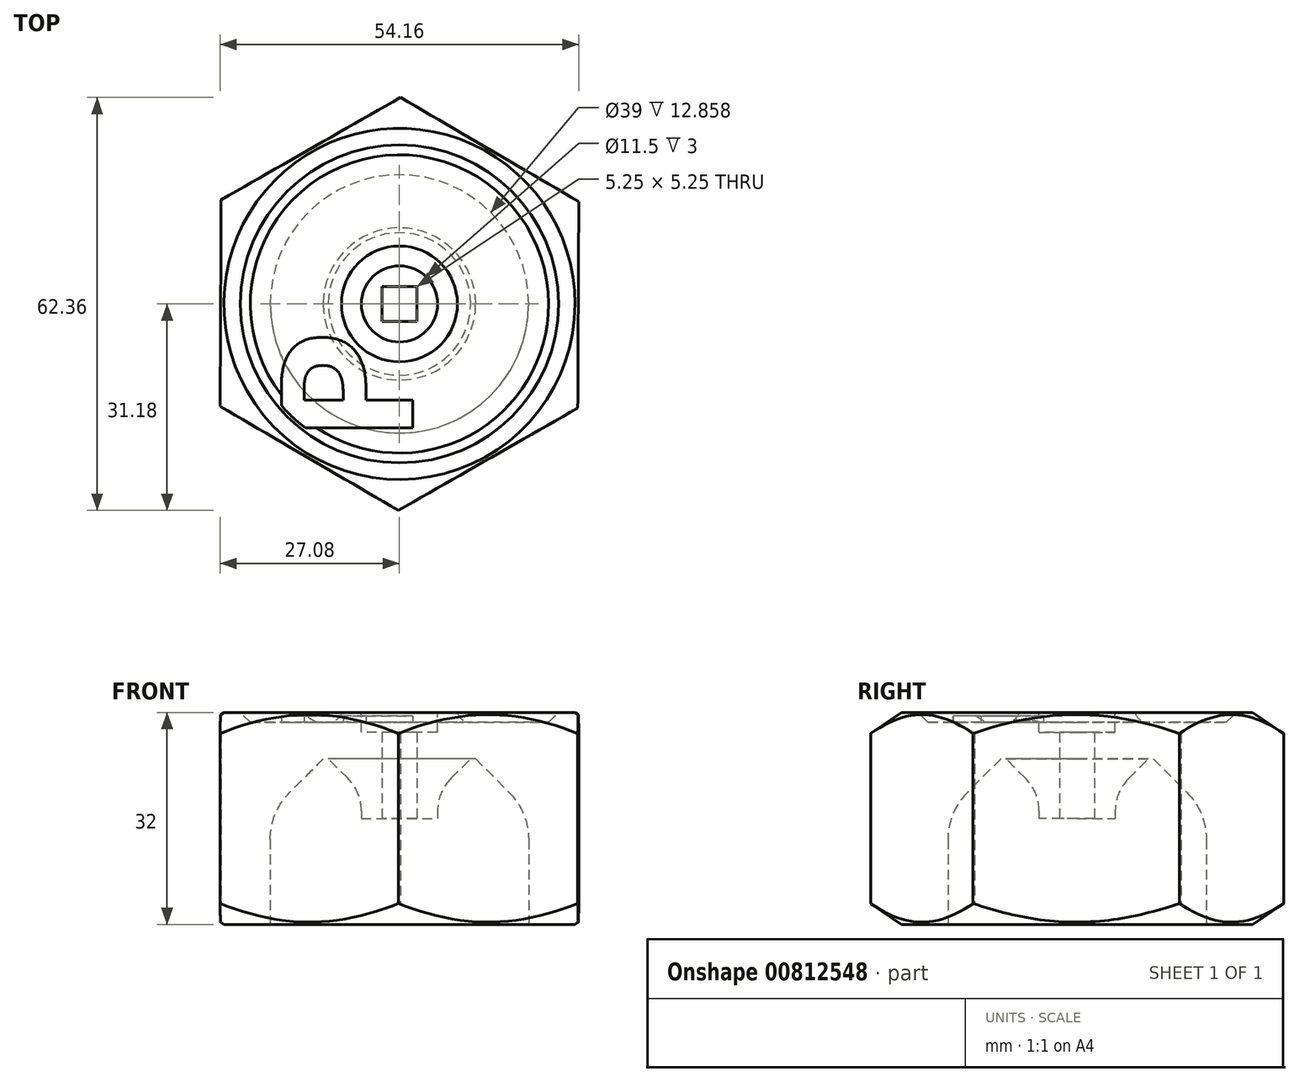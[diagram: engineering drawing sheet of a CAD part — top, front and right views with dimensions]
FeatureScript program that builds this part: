
annotation { "Feature Type Name" : "Feature", "Feature Type Description" : "" }
export const myFeature = defineFeature(function(context is Context, id is Id, definition is map)
    precondition{}
    {
        {
            var Q0;
            Q0=qCreatedBy(makeId("Top.planeOp"),FACE);
            var sketch = newSketch(context, id + "F0", { "sketchPlane" : qUnion([Q0])});
            skCircle(sketch, "E0.cCircle", {"center": v(0, 0) * mm, "radius": 27 * mm, "construction": true});
            skLineSegment(sketch, "E0.0", {"start": v(0.16, 31.18) * mm, "end": v(27.08, 15.45) * mm});
            skLineSegment(sketch, "E0.1", {"start": v(27.08, 15.45) * mm, "end": v(26.92, -15.72) * mm});
            skLineSegment(sketch, "E0.2", {"start": v(26.92, -15.72) * mm, "end": v(-0.16, -31.18) * mm});
            skLineSegment(sketch, "E0.3", {"start": v(-0.16, -31.18) * mm, "end": v(-27.08, -15.45) * mm});
            skLineSegment(sketch, "E0.4", {"start": v(-27.08, -15.45) * mm, "end": v(-26.92, 15.72) * mm});
            skLineSegment(sketch, "E0.5", {"start": v(-26.92, 15.72) * mm, "end": v(0.16, 31.18) * mm});
            skPoint(sketch, "E0.0.midPoint", {"position": v(13.62, 23.31) * mm});
            skLineSegment(sketch, "E1.bottom", {"start": v(2.63, 2.63) * mm, "end": v(-2.62, 2.63) * mm});
            skLineSegment(sketch, "E1.top", {"start": v(2.62, -2.63) * mm, "end": v(-2.62, -2.63) * mm});
            skLineSegment(sketch, "E1.left", {"start": v(2.62, 2.63) * mm, "end": v(2.62, -2.63) * mm});
            skLineSegment(sketch, "E1.right", {"start": v(-2.62, 2.62) * mm, "end": v(-2.62, -2.63) * mm});
            skCircle(sketch, "E2", {"center": v(0, 0) * mm, "radius": 5.75 * mm});
            skSolve(sketch);
        }
        {
            var Q0;
            Q0=makeQuery(id+"F0.imprint","IMPRINT",FACE,{"disambiguationData":[TD([[makeQuery(id+"F0.imprint","IMPRINT",EDGE,{"derivedFrom":sQuery(id+"F0.wireOp",EDGE,"E0.0")}),-1.0]])]});
            var Q1;
            Q1=makeQuery(id+"F0.imprint","IMPRINT",FACE,{"disambiguationData":[TD([[makeQuery(id+"F0.imprint","IMPRINT",EDGE,{"derivedFrom":sQuery(id+"F0.wireOp",EDGE,"E1.bottom")}),-1.0]])]});
            extrude(context, id + "F1", {"entities" : qUnion([Q0, Q1]), "endBound" : BoundingType.SYMMETRIC, "depth" : 32 * mm, "offsetDistance" : 25 * mm});
        }
        {
            var Q0;
            Q0=qCreatedBy(makeId("Front.planeOp"),FACE);
            var sketch = newSketch(context, id + "F2", { "sketchPlane" : qUnion([Q0])});
            skLineSegment(sketch, "E3", {"start": v(0, -34) * mm, "end": v(0, 34) * mm, "construction": true});
            skLineSegment(sketch, "E4", {"start": v(0, 34) * mm, "end": v(50.08, 0) * mm});
            skLineSegment(sketch, "E5", {"start": v(50.08, 0) * mm, "end": v(0, -34) * mm});
            skLineSegment(sketch, "E6", {"start": v(68.47, 39) * mm, "end": v(68.47, -39) * mm});
            skLineSegment(sketch, "E7", {"start": v(0, 34) * mm, "end": v(0, 39) * mm});
            skLineSegment(sketch, "E8", {"start": v(0, 39) * mm, "end": v(68.47, 39) * mm});
            skLineSegment(sketch, "E9", {"start": v(0, -34) * mm, "end": v(0, -40) * mm});
            skLineSegment(sketch, "E10", {"start": v(0, -34) * mm, "end": v(0, -39) * mm});
            skLineSegment(sketch, "E11", {"start": v(0, -39) * mm, "end": v(68.47, -39) * mm});
            skSolve(sketch);
        }
        {
            var Q0;
            Q0=qCreatedBy(makeId("Front.planeOp"),FACE);
            var sketch = newSketch(context, id + "F3", { "sketchPlane" : qUnion([Q0])});
            skLineSegment(sketch, "E12", {"start": v(0, 59.86) * mm, "end": v(0, -69.92) * mm, "construction": true});
            skSolve(sketch);
        }
        {
            var Q0;
            Q0 = qSketchRegion(id + "F2", true);
            var Q1;
            Q1=sQuery(id+"F3.wireOp",EDGE,"E12");
            revolve(context, id + "F4", {"operationType" : NewBodyOperationType.REMOVE, "surfaceOperationType" : NewSurfaceOperationType.NEW, "entities" : qUnion([Q0]), "axis" : qUnion([Q1]), "revolveType" : RevolveType.ONE_DIRECTION, "oppositeDirection" : true, "angle" : 360 * degree});
        }
        {
            var Q0;
            Q0=makeQuery(id+"F1.opExtrude","CAP_FACE",FACE,{"disambiguationData":[OSD([sQuery(id+"F0.wireOp",EDGE,"E0.0"),sQuery(id+"F0.wireOp",EDGE,"E0.1"),sQuery(id+"F0.wireOp",EDGE,"E0.2"),sQuery(id+"F0.wireOp",EDGE,"E0.3"),sQuery(id+"F0.wireOp",EDGE,"E0.4"),sQuery(id+"F0.wireOp",EDGE,"E0.5"),sQuery(id+"F0.wireOp",EDGE,"E1.bottom"),sQuery(id+"F0.wireOp",EDGE,"E1.top"),sQuery(id+"F0.wireOp",EDGE,"E1.left"),sQuery(id+"F0.wireOp",EDGE,"E1.right")])],"isStart":true});
            var sketch = newSketch(context, id + "F5", { "sketchPlane" : qUnion([Q0])});
            skCircle(sketch, "E13", {"center": v(0, 0) * mm, "radius": 19.5 * mm});
            skSolve(sketch);
        }
        {
            var Q0;
            Q0=makeQuery(id+"F5.imprint","IMPRINT",FACE,{"disambiguationData":[TD([[makeQuery(id+"F5.imprint","IMPRINT",EDGE,{"derivedFrom":sQuery(id+"F5.wireOp",EDGE,"E13")}),1.0]])]});
            var Q1;
            Q1=makeQuery(id+"F1.opExtrude","CAP_FACE",FACE,{"disambiguationData":[OSD([sQuery(id+"F0.wireOp",EDGE,"E0.0"),sQuery(id+"F0.wireOp",EDGE,"E0.1"),sQuery(id+"F0.wireOp",EDGE,"E0.2"),sQuery(id+"F0.wireOp",EDGE,"E0.3"),sQuery(id+"F0.wireOp",EDGE,"E0.4"),sQuery(id+"F0.wireOp",EDGE,"E0.5"),sQuery(id+"F0.wireOp",EDGE,"E1.bottom"),sQuery(id+"F0.wireOp",EDGE,"E1.top"),sQuery(id+"F0.wireOp",EDGE,"E1.left"),sQuery(id+"F0.wireOp",EDGE,"E1.right")])],"isStart":false});
            extrude(context, id + "F6", {"entities" : qUnion([Q0]), "operationType" : NewBodyOperationType.REMOVE, "endBound" : BoundingType.UP_TO_SURFACE, "oppositeDirection" : true, "depth" : 25 * mm, "endBoundEntityFace" : qUnion([Q1]), "hasOffset" : true, "offsetDistance" : 7 * mm});
        }
        {
            var Q0;
            Q0=makeQuery(id+"F6.boolean.opBoolean","COPY",EDGE,{"derivedFrom":makeQuery(id+"F6.opExtrude","CAP_EDGE",EDGE,{"disambiguationData":[OSD([sQuery(id+"F5.wireOp",EDGE,"E13")])],"isStart":false})});
            chamfer(context, id + "F7", {"entities" : qUnion([Q0]), "width" : 8 * mm, "tangentPropagation" : true});
        }
        {
            var Q0;
            {var subQ0=sQuery(id+"F5.wireOp",EDGE,"E13");Q0=makeQuery(id+"F7.opChamfer","BLEND_EDGE",EDGE,{"blendedFrom":[makeQuery(id+"F6.boolean.opBoolean","COPY",EDGE,{"derivedFrom":makeQuery(id+"F6.opExtrude","CAP_EDGE",EDGE,{"disambiguationData":[OSD([subQ0])],"isStart":false})}),makeQuery(id+"F6.boolean.opBoolean","COPY",FACE,{"derivedFrom":makeQuery(id+"F6.opExtrude","SWEPT_FACE",FACE,{"disambiguationData":[OSD([subQ0])]})})],"blendedInto":[makeQuery(id+"F6.boolean.opBoolean","COPY",FACE,{"derivedFrom":makeQuery(id+"F6.opExtrude","SWEPT_FACE",FACE,{"disambiguationData":[OSD([subQ0])]})})]});}
            fillet(context, id + "F8", {"entities" : qUnion([Q0]), "radius" : 10 * mm, "tangentPropagation" : true, "allowEdgeOverflow" : false});
        }
        {
            var Q0;
            Q0=makeQuery(id+"F1.opExtrude","CAP_FACE",FACE,{"disambiguationData":[OSD([sQuery(id+"F0.wireOp",EDGE,"E0.0"),sQuery(id+"F0.wireOp",EDGE,"E0.1"),sQuery(id+"F0.wireOp",EDGE,"E0.2"),sQuery(id+"F0.wireOp",EDGE,"E0.3"),sQuery(id+"F0.wireOp",EDGE,"E0.4"),sQuery(id+"F0.wireOp",EDGE,"E0.5"),sQuery(id+"F0.wireOp",EDGE,"E1.bottom"),sQuery(id+"F0.wireOp",EDGE,"E1.top"),sQuery(id+"F0.wireOp",EDGE,"E1.left"),sQuery(id+"F0.wireOp",EDGE,"E1.right")])],"isStart":false});
            var sketch = newSketch(context, id + "F9", { "sketchPlane" : qUnion([Q0])});
            skCircle(sketch, "E14.0", {"center": v(0, 0) * mm, "radius": 5.75 * mm});
            skSolve(sketch);
        }
        {
            var Q0;
            Q0 = qSketchRegion(id + "F9", true);
            extrude(context, id + "F10", {"entities" : qUnion([Q0]), "operationType" : NewBodyOperationType.REMOVE, "oppositeDirection" : true, "depth" : 5 * mm, "offsetDistance" : 25 * mm});
        }
        {
            var Q0;
            Q0=makeQuery(id+"F0.imprint","IMPRINT",FACE,{"disambiguationData":[TD([[makeQuery(id+"F0.imprint","IMPRINT",EDGE,{"derivedFrom":sQuery(id+"F0.wireOp",EDGE,"E1.bottom")}),-1.0]])]});
            var Q1;
            Q1=makeQuery(id+"F1.opExtrude","CAP_FACE",FACE,{"disambiguationData":[OSD([sQuery(id+"F0.wireOp",EDGE,"E0.0"),sQuery(id+"F0.wireOp",EDGE,"E0.1"),sQuery(id+"F0.wireOp",EDGE,"E0.2"),sQuery(id+"F0.wireOp",EDGE,"E0.3"),sQuery(id+"F0.wireOp",EDGE,"E0.4"),sQuery(id+"F0.wireOp",EDGE,"E0.5"),sQuery(id+"F0.wireOp",EDGE,"E1.bottom"),sQuery(id+"F0.wireOp",EDGE,"E1.top"),sQuery(id+"F0.wireOp",EDGE,"E1.left"),sQuery(id+"F0.wireOp",EDGE,"E1.right")])],"isStart":false});
            extrude(context, id + "F11", {"entities" : qUnion([Q0]), "operationType" : NewBodyOperationType.ADD, "endBound" : BoundingType.UP_TO_SURFACE, "depth" : 25 * mm, "endBoundEntityFace" : qUnion([Q1]), "hasOffset" : true, "offsetDistance" : 3 * mm});
        }
        {
            var Q0;
            Q0=makeQuery(id+"F11.boolean.opBoolean","INTERSECT",EDGE,{"derivedFrom":[makeQuery(id+"F6.boolean.opBoolean","COPY",FACE,{"derivedFrom":makeQuery(id+"F6.opExtrude","CAP_FACE",FACE,{"disambiguationData":[OSD([sQuery(id+"F0.wireOp",EDGE,"E1.bottom"),sQuery(id+"F0.wireOp",EDGE,"E1.top"),sQuery(id+"F0.wireOp",EDGE,"E1.left"),sQuery(id+"F0.wireOp",EDGE,"E1.right"),sQuery(id+"F5.wireOp",EDGE,"E13")])],"isStart":false})}),makeQuery(id+"F11.opExtrude","SWEPT_FACE",FACE,{"disambiguationData":[OSD([sQuery(id+"F0.wireOp",EDGE,"E2")])]})]});
            chamfer(context, id + "F12", {"entities" : qUnion([Q0]), "width" : 5 * mm, "tangentPropagation" : true});
        }
        {
            var Q0;
            {var subQ0=makeQuery(id+"F11.opExtrude","SWEPT_FACE",FACE,{"disambiguationData":[OSD([sQuery(id+"F0.wireOp",EDGE,"E2")])]});Q0=makeQuery(id+"F12.opChamfer","BLEND_EDGE",EDGE,{"blendedFrom":[makeQuery(id+"F11.boolean.opBoolean","INTERSECT",EDGE,{"derivedFrom":[makeQuery(id+"F6.boolean.opBoolean","COPY",FACE,{"derivedFrom":makeQuery(id+"F6.opExtrude","CAP_FACE",FACE,{"disambiguationData":[OSD([sQuery(id+"F0.wireOp",EDGE,"E1.bottom"),sQuery(id+"F0.wireOp",EDGE,"E1.top"),sQuery(id+"F0.wireOp",EDGE,"E1.left"),sQuery(id+"F0.wireOp",EDGE,"E1.right"),sQuery(id+"F5.wireOp",EDGE,"E13")])],"isStart":false})}),subQ0]}),subQ0],"blendedInto":[subQ0]});}
            fillet(context, id + "F13", {"entities" : qUnion([Q0]), "radius" : 7 * mm, "tangentPropagation" : true, "allowEdgeOverflow" : false});
        }
        {
            var Q0;
            Q0=makeQuery(id+"F1.opExtrude","CAP_FACE",FACE,{"disambiguationData":[OSD([sQuery(id+"F0.wireOp",EDGE,"E0.0"),sQuery(id+"F0.wireOp",EDGE,"E0.1"),sQuery(id+"F0.wireOp",EDGE,"E0.2"),sQuery(id+"F0.wireOp",EDGE,"E0.3"),sQuery(id+"F0.wireOp",EDGE,"E0.4"),sQuery(id+"F0.wireOp",EDGE,"E0.5"),sQuery(id+"F0.wireOp",EDGE,"E1.bottom"),sQuery(id+"F0.wireOp",EDGE,"E1.top"),sQuery(id+"F0.wireOp",EDGE,"E1.left"),sQuery(id+"F0.wireOp",EDGE,"E1.right")])],"isStart":false});
            var sketch = newSketch(context, id + "F14", { "sketchPlane" : qUnion([Q0])});
            skCircle(sketch, "E15", {"center": v(0, 0) * mm, "radius": 24.51 * mm});
            skCircle(sketch, "E16", {"center": v(0, 0) * mm, "radius": 8.75 * mm});
            skSolve(sketch);
        }
        {
            var Q0;
            Q0=makeQuery(id+"F14.imprint","IMPRINT",FACE,{"disambiguationData":[TD([[makeQuery(id+"F14.imprint","IMPRINT",EDGE,{"derivedFrom":sQuery(id+"F14.wireOp",EDGE,"E15")}),1.0]])]});
            extrude(context, id + "F15", {"entities" : qUnion([Q0]), "operationType" : NewBodyOperationType.REMOVE, "oppositeDirection" : true, "depth" : 1.5 * mm, "offsetDistance" : 25 * mm});
        }
        {
            var Q0;
            Q0=makeQuery(id+"F15.boolean.opBoolean","COPY",EDGE,{"derivedFrom":makeQuery(id+"F15.opExtrude","CAP_EDGE",EDGE,{"disambiguationData":[OSD([sQuery(id+"F14.wireOp",EDGE,"E15")])],"isStart":false})});
            chamfer(context, id + "F16", {"entities" : qUnion([Q0]), "width" : 2 * mm, "tangentPropagation" : true});
        }
        {
            var Q0;
            Q0=makeQuery(id+"F15.boolean.opBoolean","COPY",EDGE,{"derivedFrom":makeQuery(id+"F15.opExtrude","CAP_EDGE",EDGE,{"disambiguationData":[OSD([sQuery(id+"F14.wireOp",EDGE,"E16")])],"isStart":false})});
            fillet(context, id + "F17", {"entities" : qUnion([Q0]), "radius" : 2 * mm, "tangentPropagation" : true, "allowEdgeOverflow" : false});
        }
        {
            var Q0;
            Q0=makeQuery(id+"F15.boolean.opBoolean","COPY",FACE,{"derivedFrom":makeQuery(id+"F15.opExtrude","CAP_FACE",FACE,{"disambiguationData":[OSD([sQuery(id+"F14.wireOp",EDGE,"E15"),sQuery(id+"F14.wireOp",EDGE,"E16")])],"isStart":false})});
            var sketch = newSketch(context, id + "F18", { "sketchPlane" : qUnion([Q0])});
            skText(sketch, "E17", { "text": "P", "fontName": "OpenSans-Bold.ttf"});
            const initialGuessF18  = {"E17": [0.002, -0.02123, 0, 1, 0.02]};
            skSetInitialGuess(sketch, initialGuessF18);
            skSolve(sketch);
        }
        {
            var Q0;
            Q0 = qSketchRegion(id + "F18", true);
            var Q1;
            Q1=makeQuery(id+"F15.boolean.opBoolean","COPY",FACE,{"derivedFrom":makeQuery(id+"F15.opExtrude","CAP_FACE",FACE,{"disambiguationData":[OSD([sQuery(id+"F14.wireOp",EDGE,"E15"),sQuery(id+"F14.wireOp",EDGE,"E16")])],"isStart":false})});
            extrude(context, id + "F19", {"entities" : qUnion([Q0]), "operationType" : NewBodyOperationType.ADD, "depth" : 1 * mm, "endBoundEntityFace" : qUnion([Q1]), "offsetDistance" : 25 * mm});
        }
    });
